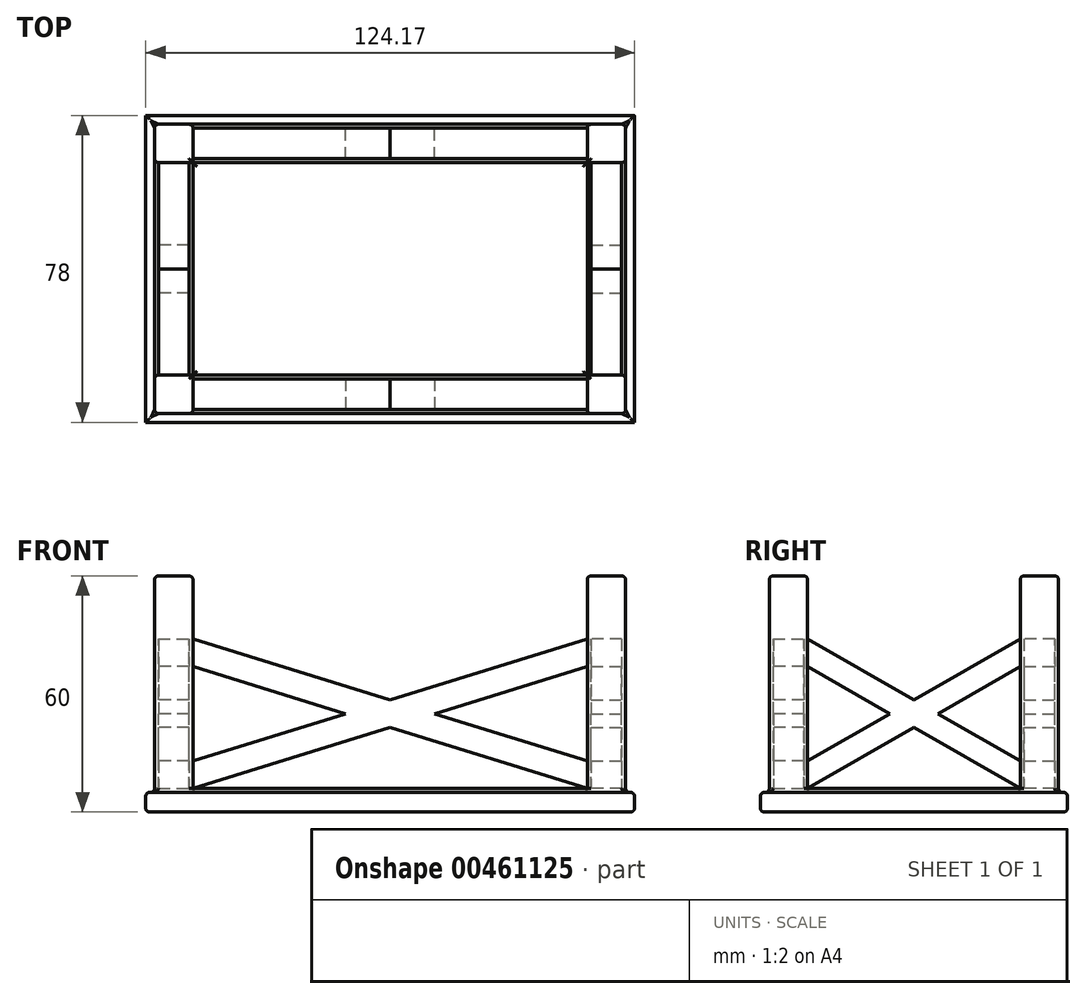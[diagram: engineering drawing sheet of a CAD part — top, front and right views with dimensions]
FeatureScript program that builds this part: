
annotation { "Feature Type Name" : "Feature", "Feature Type Description" : "" }
export const myFeature = defineFeature(function(context is Context, id is Id, definition is map)
    precondition{}
    {
        {
            var Q0;
            Q0=qCreatedBy(makeId("Top.planeOp"),FACE);
            var sketch = newSketch(context, id + "F0", { "sketchPlane" : qUnion([Q0])});
            skLineSegment(sketch, "E0.bottom", {"start": v(-35.73, 48.82) * mm, "end": v(88.44, 48.82) * mm});
            skLineSegment(sketch, "E0.top", {"start": v(-35.73, -29.18) * mm, "end": v(88.44, -29.18) * mm});
            skLineSegment(sketch, "E0.left", {"start": v(-35.73, 48.82) * mm, "end": v(-35.73, -29.18) * mm});
            skLineSegment(sketch, "E0.right", {"start": v(88.44, 48.82) * mm, "end": v(88.44, -29.18) * mm});
            skPoint(sketch, "E1", {"position": v(26.36, -29.18) * mm});
            skSolve(sketch);
        }
        {
            var Q0;
            Q0 = qSketchRegion(id + "F0", true);
            extrude(context, id + "F1", {"entities" : qUnion([Q0]), "depth" : 5 * mm});
        }
        {
            var Q0;
            Q0=makeQuery(id+"F1.opExtrude","CAP_FACE",FACE,{"disambiguationData":[OSD([sQuery(id+"F0.wireOp",EDGE,"E0.bottom"),sQuery(id+"F0.wireOp",EDGE,"E0.top"),sQuery(id+"F0.wireOp",EDGE,"E0.left"),sQuery(id+"F0.wireOp",EDGE,"E0.right")])],"isStart":false});
            var sketch = newSketch(context, id + "F2", { "sketchPlane" : qUnion([Q0])});
            skLineSegment(sketch, "E2.bottom", {"start": v(-35.73, -29.18) * mm, "end": v(-23.73, -29.18) * mm, "construction": true});
            skLineSegment(sketch, "E2.top", {"start": v(-35.73, -17.18) * mm, "end": v(-23.73, -17.18) * mm, "construction": true});
            skLineSegment(sketch, "E2.left", {"start": v(-35.73, -29.18) * mm, "end": v(-35.73, -17.18) * mm, "construction": true});
            skLineSegment(sketch, "E2.right", {"start": v(-23.73, -29.18) * mm, "end": v(-23.73, -17.18) * mm, "construction": true});
            skLineSegment(sketch, "E3.bottom", {"start": v(88.44, 48.82) * mm, "end": v(76.44, 48.82) * mm, "construction": true});
            skLineSegment(sketch, "E3.top", {"start": v(88.44, 36.82) * mm, "end": v(76.44, 36.82) * mm, "construction": true});
            skLineSegment(sketch, "E3.left", {"start": v(88.44, 48.82) * mm, "end": v(88.44, 36.82) * mm, "construction": true});
            skLineSegment(sketch, "E3.right", {"start": v(76.44, 48.82) * mm, "end": v(76.44, 36.82) * mm, "construction": true});
            skLineSegment(sketch, "E4.bottom", {"start": v(88.44, -29.18) * mm, "end": v(76.44, -29.18) * mm, "construction": true});
            skLineSegment(sketch, "E4.top", {"start": v(88.44, -17.18) * mm, "end": v(76.44, -17.18) * mm, "construction": true});
            skLineSegment(sketch, "E4.left", {"start": v(88.44, -29.18) * mm, "end": v(88.44, -17.18) * mm, "construction": true});
            skLineSegment(sketch, "E4.right", {"start": v(76.44, -29.18) * mm, "end": v(76.44, -17.18) * mm, "construction": true});
            skLineSegment(sketch, "E5.bottom", {"start": v(-35.73, 48.82) * mm, "end": v(-23.73, 48.82) * mm, "construction": true});
            skLineSegment(sketch, "E5.top", {"start": v(-35.73, 36.82) * mm, "end": v(-23.73, 36.82) * mm, "construction": true});
            skLineSegment(sketch, "E5.left", {"start": v(-35.73, 48.82) * mm, "end": v(-35.73, 36.82) * mm, "construction": true});
            skLineSegment(sketch, "E5.right", {"start": v(-23.73, 48.82) * mm, "end": v(-23.73, 36.82) * mm, "construction": true});
            skLineSegment(sketch, "E6.bottom", {"start": v(-23.73, 36.82) * mm, "end": v(-33.48, 36.82) * mm});
            skLineSegment(sketch, "E6.top", {"start": v(-23.73, 46.57) * mm, "end": v(-33.48, 46.57) * mm});
            skLineSegment(sketch, "E6.left", {"start": v(-23.73, 36.82) * mm, "end": v(-23.73, 46.57) * mm});
            skLineSegment(sketch, "E6.right", {"start": v(-33.48, 36.82) * mm, "end": v(-33.48, 46.57) * mm});
            skLineSegment(sketch, "E7.bottom", {"start": v(-23.73, -17.18) * mm, "end": v(-33.48, -17.18) * mm});
            skLineSegment(sketch, "E7.top", {"start": v(-23.73, -26.93) * mm, "end": v(-33.48, -26.93) * mm});
            skLineSegment(sketch, "E7.left", {"start": v(-23.73, -17.18) * mm, "end": v(-23.73, -26.93) * mm});
            skLineSegment(sketch, "E7.right", {"start": v(-33.48, -17.18) * mm, "end": v(-33.48, -26.93) * mm});
            skLineSegment(sketch, "E8.bottom", {"start": v(76.44, 36.82) * mm, "end": v(86.2, 36.82) * mm});
            skLineSegment(sketch, "E8.top", {"start": v(76.44, 46.57) * mm, "end": v(86.2, 46.57) * mm});
            skLineSegment(sketch, "E8.left", {"start": v(76.44, 36.82) * mm, "end": v(76.44, 46.57) * mm});
            skLineSegment(sketch, "E8.right", {"start": v(86.2, 36.82) * mm, "end": v(86.2, 46.57) * mm});
            skLineSegment(sketch, "E9.bottom", {"start": v(76.44, -17.18) * mm, "end": v(86.2, -17.18) * mm});
            skLineSegment(sketch, "E9.top", {"start": v(76.44, -26.93) * mm, "end": v(86.2, -26.93) * mm});
            skLineSegment(sketch, "E9.left", {"start": v(76.44, -17.18) * mm, "end": v(76.44, -26.93) * mm});
            skLineSegment(sketch, "E9.right", {"start": v(86.2, -17.18) * mm, "end": v(86.2, -26.93) * mm});
            skSolve(sketch);
        }
        {
            var Q0;
            Q0 = qSketchRegion(id + "F2", true);
            extrude(context, id + "F3", {"entities" : qUnion([Q0]), "operationType" : NewBodyOperationType.ADD, "depth" : 55 * mm});
        }
        {
            var Q0;
            Q0=makeQuery(id+"F3.opExtrude","SWEPT_FACE",FACE,{"disambiguationData":[OSD([sQuery(id+"F2.wireOp",EDGE,"E7.left")])]});
            var sketch = newSketch(context, id + "F4", { "sketchPlane" : qUnion([Q0])});
            skLineSegment(sketch, "E10.bottom", {"start": v(-25.93, 59) * mm, "end": v(-18.18, 59) * mm, "construction": true});
            skLineSegment(sketch, "E10.top", {"start": v(-25.93, 44) * mm, "end": v(-18.18, 44) * mm, "construction": true});
            skLineSegment(sketch, "E10.left", {"start": v(-25.93, 59) * mm, "end": v(-25.93, 44) * mm, "construction": true});
            skLineSegment(sketch, "E10.right", {"start": v(-18.18, 59) * mm, "end": v(-18.18, 44) * mm, "construction": true});
            skLineSegment(sketch, "E11.bottom", {"start": v(-25.93, 44) * mm, "end": v(-18.18, 44) * mm});
            skLineSegment(sketch, "E11.top", {"start": v(-25.93, 6) * mm, "end": v(-18.18, 6) * mm});
            skLineSegment(sketch, "E11.left", {"start": v(-25.93, 44) * mm, "end": v(-25.93, 6) * mm});
            skLineSegment(sketch, "E11.right", {"start": v(-18.18, 44) * mm, "end": v(-18.18, 6) * mm});
            skSolve(sketch);
        }
        {
            var Q0;
            Q0 = qSketchRegion(id + "F4", true);
            extrude(context, id + "F5", {"entities" : qUnion([Q0]), "operationType" : NewBodyOperationType.ADD, "endBound" : BoundingType.UP_TO_NEXT, "depth" : 100.17 * mm});
        }
        {
            var Q0;
            Q0=makeQuery(id+"F5.opExtrude","SWEPT_FACE",FACE,{"disambiguationData":[OSD([sQuery(id+"F4.wireOp",EDGE,"E11.left")])]});
            var sketch = newSketch(context, id + "F6", { "sketchPlane" : qUnion([Q0])});
            skPoint(sketch, "E12", {"position": v(-23.73, 44) * mm});
            skPoint(sketch, "E13", {"position": v(-23.73, 37) * mm});
            skPoint(sketch, "E14", {"position": v(-23.73, 6) * mm});
            skPoint(sketch, "E15", {"position": v(-23.73, 13) * mm});
            skPoint(sketch, "E16", {"position": v(76.44, 44) * mm});
            skPoint(sketch, "E17", {"position": v(76.44, 37) * mm});
            skPoint(sketch, "E18", {"position": v(76.44, 6) * mm});
            skPoint(sketch, "E19", {"position": v(76.44, 13) * mm});
            skPoint(sketch, "E20", {"position": v(26.36, 28.5) * mm});
            skPoint(sketch, "E21", {"position": v(26.36, 21.5) * mm});
            skPoint(sketch, "E22", {"position": v(15.05, 25) * mm});
            skPoint(sketch, "E23", {"position": v(37.67, 25) * mm});
            skLineSegment(sketch, "E24", {"start": v(-23.73, 44) * mm, "end": v(76.44, 44) * mm});
            skLineSegment(sketch, "E25", {"start": v(26.36, 28.5) * mm, "end": v(76.44, 44) * mm});
            skLineSegment(sketch, "E26", {"start": v(-23.73, 44) * mm, "end": v(26.36, 28.5) * mm});
            skLineSegment(sketch, "E27", {"start": v(76.44, 37) * mm, "end": v(76.44, 13) * mm});
            skLineSegment(sketch, "E28", {"start": v(76.44, 13.06) * mm, "end": v(37.67, 25) * mm});
            skLineSegment(sketch, "E29", {"start": v(15.05, 25) * mm, "end": v(-23.73, 37) * mm});
            skLineSegment(sketch, "E30", {"start": v(15.05, 25) * mm, "end": v(-23.73, 13) * mm});
            skLineSegment(sketch, "E31", {"start": v(-23.73, 13) * mm, "end": v(-23.73, 37) * mm});
            skLineSegment(sketch, "E32", {"start": v(-23.73, 6) * mm, "end": v(76.44, 6) * mm});
            skLineSegment(sketch, "E33", {"start": v(26.36, 21.5) * mm, "end": v(76.44, 6) * mm});
            skLineSegment(sketch, "E34", {"start": v(26.36, 21.5) * mm, "end": v(-23.73, 6) * mm});
            skLineSegment(sketch, "E35", {"start": v(37.67, 25) * mm, "end": v(76.44, 37) * mm});
            skLineSegment(sketch, "E36", {"start": v(76.44, 37) * mm, "end": v(76.44, 13.06) * mm});
            skSolve(sketch);
        }
        {
            var Q0;
            Q0 = qSketchRegion(id + "F6", true);
            extrude(context, id + "F7", {"entities" : qUnion([Q0]), "operationType" : NewBodyOperationType.REMOVE, "endBound" : BoundingType.UP_TO_NEXT, "oppositeDirection" : true, "depth" : 25 * mm});
        }
        {
            var Q0;
            Q0=makeQuery(id+"F3.opExtrude","SWEPT_FACE",FACE,{"disambiguationData":[OSD([sQuery(id+"F2.wireOp",EDGE,"E8.left")])]});
            var sketch = newSketch(context, id + "F8", { "sketchPlane" : qUnion([Q0])});
            skLineSegment(sketch, "E37.bottom", {"start": v(-45.57, 59) * mm, "end": v(-37.82, 59) * mm, "construction": true});
            skLineSegment(sketch, "E37.top", {"start": v(-45.57, 44) * mm, "end": v(-37.82, 44) * mm, "construction": true});
            skLineSegment(sketch, "E37.left", {"start": v(-45.57, 59) * mm, "end": v(-45.57, 44) * mm, "construction": true});
            skLineSegment(sketch, "E37.right", {"start": v(-37.82, 59) * mm, "end": v(-37.82, 44) * mm, "construction": true});
            skLineSegment(sketch, "E38.bottom", {"start": v(-45.57, 44) * mm, "end": v(-37.82, 44) * mm});
            skLineSegment(sketch, "E38.top", {"start": v(-45.57, 6) * mm, "end": v(-37.82, 6) * mm});
            skLineSegment(sketch, "E38.left", {"start": v(-45.57, 44) * mm, "end": v(-45.57, 6) * mm});
            skLineSegment(sketch, "E38.right", {"start": v(-37.82, 44) * mm, "end": v(-37.82, 6) * mm});
            skSolve(sketch);
        }
        {
            var Q0;
            Q0 = qSketchRegion(id + "F8", true);
            extrude(context, id + "F9", {"entities" : qUnion([Q0]), "operationType" : NewBodyOperationType.ADD, "endBound" : BoundingType.UP_TO_NEXT, "depth" : 25 * mm});
        }
        {
            var Q0;
            Q0=makeQuery(id+"F9.opExtrude","SWEPT_FACE",FACE,{"disambiguationData":[OSD([sQuery(id+"F8.wireOp",EDGE,"E38.left")])]});
            var sketch = newSketch(context, id + "F10", { "sketchPlane" : qUnion([Q0])});
            skPoint(sketch, "E39", {"position": v(-76.44, 44) * mm});
            skPoint(sketch, "E40", {"position": v(-76.44, 37) * mm});
            skPoint(sketch, "E41", {"position": v(-76.44, 13) * mm});
            skPoint(sketch, "E42", {"position": v(-76.44, 6) * mm});
            skPoint(sketch, "E43", {"position": v(23.73, 44) * mm});
            skPoint(sketch, "E44", {"position": v(23.73, 37) * mm});
            skPoint(sketch, "E45", {"position": v(23.73, 13) * mm});
            skPoint(sketch, "E46", {"position": v(23.73, 6) * mm});
            skLineSegment(sketch, "E47", {"start": v(-76.44, 37) * mm, "end": v(23.73, 6) * mm, "construction": true});
            skLineSegment(sketch, "E48", {"start": v(-76.44, 44) * mm, "end": v(23.73, 13) * mm, "construction": true});
            skLineSegment(sketch, "E49", {"start": v(23.73, 44) * mm, "end": v(-76.44, 13) * mm, "construction": true});
            skLineSegment(sketch, "E50", {"start": v(-76.44, 6) * mm, "end": v(23.73, 37) * mm, "construction": true});
            skLineSegment(sketch, "E51", {"start": v(-76.44, 44) * mm, "end": v(-26.36, 28.5) * mm});
            skLineSegment(sketch, "E52", {"start": v(-26.36, 28.5) * mm, "end": v(23.73, 44) * mm});
            skLineSegment(sketch, "E53", {"start": v(-76.44, 44) * mm, "end": v(23.73, 44) * mm});
            skLineSegment(sketch, "E54", {"start": v(-76.44, 13) * mm, "end": v(-76.44, 37) * mm});
            skLineSegment(sketch, "E55", {"start": v(-76.44, 37) * mm, "end": v(-37.67, 25) * mm});
            skLineSegment(sketch, "E56", {"start": v(-37.67, 25) * mm, "end": v(-76.44, 13) * mm});
            skLineSegment(sketch, "E57", {"start": v(-76.44, 6) * mm, "end": v(23.73, 6) * mm});
            skLineSegment(sketch, "E58", {"start": v(-26.36, 21.5) * mm, "end": v(23.73, 6) * mm});
            skLineSegment(sketch, "E59", {"start": v(-76.44, 6) * mm, "end": v(-26.36, 21.5) * mm});
            skLineSegment(sketch, "E60", {"start": v(23.73, 37) * mm, "end": v(23.73, 13) * mm});
            skLineSegment(sketch, "E61", {"start": v(23.73, 13) * mm, "end": v(-15.05, 25) * mm});
            skLineSegment(sketch, "E62", {"start": v(-15.05, 25) * mm, "end": v(23.73, 37) * mm});
            skSolve(sketch);
        }
        {
            var Q0;
            Q0 = qSketchRegion(id + "F10", true);
            extrude(context, id + "F11", {"entities" : qUnion([Q0]), "operationType" : NewBodyOperationType.REMOVE, "endBound" : BoundingType.UP_TO_NEXT, "oppositeDirection" : true, "depth" : 25 * mm});
        }
        {
            var Q0;
            Q0=makeQuery(id+"F3.opExtrude","SWEPT_FACE",FACE,{"disambiguationData":[OSD([sQuery(id+"F2.wireOp",EDGE,"E6.bottom")])]});
            var sketch = newSketch(context, id + "F12", { "sketchPlane" : qUnion([Q0])});
            skLineSegment(sketch, "E63.bottom", {"start": v(-32.48, 59) * mm, "end": v(-24.73, 59) * mm, "construction": true});
            skLineSegment(sketch, "E63.top", {"start": v(-32.48, 44) * mm, "end": v(-24.73, 44) * mm, "construction": true});
            skLineSegment(sketch, "E63.left", {"start": v(-32.48, 59) * mm, "end": v(-32.48, 44) * mm, "construction": true});
            skLineSegment(sketch, "E63.right", {"start": v(-24.73, 59) * mm, "end": v(-24.73, 44) * mm, "construction": true});
            skLineSegment(sketch, "E64.bottom", {"start": v(-32.48, 44) * mm, "end": v(-24.73, 44) * mm});
            skLineSegment(sketch, "E64.top", {"start": v(-32.48, 6) * mm, "end": v(-24.73, 6) * mm});
            skLineSegment(sketch, "E64.left", {"start": v(-32.48, 44) * mm, "end": v(-32.48, 6) * mm});
            skLineSegment(sketch, "E64.right", {"start": v(-24.73, 44) * mm, "end": v(-24.73, 6) * mm});
            skSolve(sketch);
        }
        {
            var Q0;
            Q0 = qSketchRegion(id + "F12", true);
            extrude(context, id + "F13", {"entities" : qUnion([Q0]), "operationType" : NewBodyOperationType.ADD, "endBound" : BoundingType.UP_TO_NEXT, "depth" : 25 * mm});
        }
        {
            var Q0;
            Q0=makeQuery(id+"F13.opExtrude","SWEPT_FACE",FACE,{"disambiguationData":[OSD([sQuery(id+"F12.wireOp",EDGE,"E64.left")])]});
            var sketch = newSketch(context, id + "F14", { "sketchPlane" : qUnion([Q0])});
            skPoint(sketch, "E65", {"position": v(-36.82, 44) * mm});
            skPoint(sketch, "E66", {"position": v(-36.82, 37) * mm});
            skPoint(sketch, "E67", {"position": v(-36.82, 13) * mm});
            skPoint(sketch, "E68", {"position": v(-36.82, 6) * mm});
            skPoint(sketch, "E69", {"position": v(17.18, 6) * mm});
            skPoint(sketch, "E70", {"position": v(17.18, 13) * mm});
            skPoint(sketch, "E71", {"position": v(17.18, 37) * mm});
            skPoint(sketch, "E72", {"position": v(17.18, 44) * mm});
            skLineSegment(sketch, "E73", {"start": v(-36.82, 37) * mm, "end": v(17.18, 6) * mm, "construction": true});
            skLineSegment(sketch, "E74", {"start": v(17.18, 13) * mm, "end": v(-36.82, 44) * mm, "construction": true});
            skLineSegment(sketch, "E75", {"start": v(-36.82, 13) * mm, "end": v(17.18, 44) * mm, "construction": true});
            skLineSegment(sketch, "E76", {"start": v(17.18, 37) * mm, "end": v(-36.82, 6) * mm, "construction": true});
            skLineSegment(sketch, "E77", {"start": v(-36.82, 44) * mm, "end": v(17.18, 44) * mm});
            skLineSegment(sketch, "E78", {"start": v(-9.82, 28.5) * mm, "end": v(17.18, 44) * mm});
            skLineSegment(sketch, "E79", {"start": v(-9.82, 28.5) * mm, "end": v(-36.82, 44) * mm});
            skLineSegment(sketch, "E80", {"start": v(-36.82, 37) * mm, "end": v(-36.82, 13) * mm});
            skLineSegment(sketch, "E81", {"start": v(-36.82, 13) * mm, "end": v(-15.92, 25) * mm});
            skLineSegment(sketch, "E82", {"start": v(-15.92, 25) * mm, "end": v(-36.82, 37) * mm});
            skLineSegment(sketch, "E83", {"start": v(17.18, 37) * mm, "end": v(17.18, 13) * mm});
            skLineSegment(sketch, "E84", {"start": v(17.18, 13) * mm, "end": v(-3.72, 25) * mm});
            skLineSegment(sketch, "E85", {"start": v(17.18, 37) * mm, "end": v(-3.72, 25) * mm});
            skLineSegment(sketch, "E86", {"start": v(-36.82, 6) * mm, "end": v(17.18, 6) * mm});
            skLineSegment(sketch, "E87", {"start": v(17.18, 6) * mm, "end": v(-9.82, 21.5) * mm});
            skLineSegment(sketch, "E88", {"start": v(-36.82, 6) * mm, "end": v(-9.82, 21.5) * mm});
            skSolve(sketch);
        }
        {
            var Q0;
            Q0 = qSketchRegion(id + "F14", true);
            extrude(context, id + "F15", {"entities" : qUnion([Q0]), "operationType" : NewBodyOperationType.REMOVE, "endBound" : BoundingType.UP_TO_NEXT, "oppositeDirection" : true, "depth" : 25 * mm});
        }
        {
            var Q0;
            Q0=makeQuery(id+"F3.opExtrude","SWEPT_FACE",FACE,{"disambiguationData":[OSD([sQuery(id+"F2.wireOp",EDGE,"E9.bottom")])]});
            var sketch = newSketch(context, id + "F16", { "sketchPlane" : qUnion([Q0])});
            skLineSegment(sketch, "E89.bottom", {"start": v(-85.2, 59) * mm, "end": v(-77.44, 59) * mm, "construction": true});
            skLineSegment(sketch, "E89.top", {"start": v(-85.2, 44) * mm, "end": v(-77.44, 44) * mm, "construction": true});
            skLineSegment(sketch, "E89.left", {"start": v(-85.2, 59) * mm, "end": v(-85.2, 44) * mm, "construction": true});
            skLineSegment(sketch, "E89.right", {"start": v(-77.44, 59) * mm, "end": v(-77.44, 44) * mm, "construction": true});
            skLineSegment(sketch, "E90.bottom", {"start": v(-85.2, 44) * mm, "end": v(-77.44, 44) * mm});
            skLineSegment(sketch, "E90.top", {"start": v(-85.2, 6) * mm, "end": v(-77.44, 6) * mm});
            skLineSegment(sketch, "E90.left", {"start": v(-85.2, 44) * mm, "end": v(-85.2, 6) * mm});
            skLineSegment(sketch, "E90.right", {"start": v(-77.44, 44) * mm, "end": v(-77.44, 6) * mm});
            skSolve(sketch);
        }
        {
            var Q0;
            Q0 = qSketchRegion(id + "F16", true);
            extrude(context, id + "F17", {"entities" : qUnion([Q0]), "operationType" : NewBodyOperationType.ADD, "endBound" : BoundingType.UP_TO_NEXT, "depth" : 25 * mm});
        }
        {
            var Q0;
            Q0=makeQuery(id+"F17.opExtrude","SWEPT_FACE",FACE,{"disambiguationData":[OSD([sQuery(id+"F16.wireOp",EDGE,"E90.left")])]});
            var sketch = newSketch(context, id + "F18", { "sketchPlane" : qUnion([Q0])});
            skPoint(sketch, "E91", {"position": v(-17.18, 44) * mm});
            skPoint(sketch, "E92", {"position": v(-17.18, 37) * mm});
            skPoint(sketch, "E93", {"position": v(-17.18, 13) * mm});
            skPoint(sketch, "E94", {"position": v(-17.18, 6) * mm});
            skPoint(sketch, "E95", {"position": v(36.82, 44) * mm});
            skPoint(sketch, "E96", {"position": v(36.82, 37) * mm});
            skPoint(sketch, "E97", {"position": v(36.82, 13) * mm});
            skPoint(sketch, "E98", {"position": v(36.82, 6) * mm});
            skLineSegment(sketch, "E99", {"start": v(-17.18, 44) * mm, "end": v(36.82, 13) * mm, "construction": true});
            skLineSegment(sketch, "E100", {"start": v(36.82, 6) * mm, "end": v(-17.18, 37) * mm, "construction": true});
            skLineSegment(sketch, "E101", {"start": v(36.82, 44) * mm, "end": v(-17.18, 13) * mm, "construction": true});
            skLineSegment(sketch, "E102", {"start": v(-17.18, 6) * mm, "end": v(36.82, 37) * mm, "construction": true});
            skLineSegment(sketch, "E103", {"start": v(-17.18, 44) * mm, "end": v(36.82, 44) * mm});
            skLineSegment(sketch, "E104", {"start": v(36.82, 44) * mm, "end": v(9.82, 28.5) * mm});
            skLineSegment(sketch, "E105", {"start": v(9.82, 28.5) * mm, "end": v(-17.18, 44) * mm});
            skLineSegment(sketch, "E106", {"start": v(-17.18, 37) * mm, "end": v(-17.18, 13) * mm});
            skLineSegment(sketch, "E107", {"start": v(-17.18, 13) * mm, "end": v(3.72, 25) * mm});
            skLineSegment(sketch, "E108", {"start": v(-17.18, 37) * mm, "end": v(3.72, 25) * mm});
            skLineSegment(sketch, "E109", {"start": v(36.82, 37) * mm, "end": v(36.82, 13) * mm});
            skLineSegment(sketch, "E110", {"start": v(36.82, 13) * mm, "end": v(15.92, 25) * mm});
            skLineSegment(sketch, "E111", {"start": v(15.92, 25) * mm, "end": v(36.82, 37) * mm});
            skLineSegment(sketch, "E112", {"start": v(-17.18, 6) * mm, "end": v(36.82, 6) * mm});
            skLineSegment(sketch, "E113", {"start": v(36.82, 6) * mm, "end": v(9.82, 21.5) * mm});
            skLineSegment(sketch, "E114", {"start": v(9.82, 21.5) * mm, "end": v(-17.18, 6) * mm});
            skSolve(sketch);
        }
        {
            var Q0;
            Q0 = qSketchRegion(id + "F18", true);
            extrude(context, id + "F19", {"entities" : qUnion([Q0]), "operationType" : NewBodyOperationType.REMOVE, "endBound" : BoundingType.UP_TO_NEXT, "oppositeDirection" : true, "depth" : 25 * mm});
        }
        {
            var Q0;
            Q0=makeQuery(id+"F15.boolean.opBoolean","MERGE",FACE,{"derivedFrom":[makeQuery(id+"F3.opExtrude","SWEPT_FACE",FACE,{"disambiguationData":[OSD([sQuery(id+"F2.wireOp",EDGE,"E7.bottom")])]}),makeQuery(id+"F15.opExtrude","SWEPT_FACE",FACE,{"disambiguationData":[OSD([sQuery(id+"F14.wireOp",EDGE,"E83")])]})]});
            var sketch = newSketch(context, id + "F20", { "sketchPlane" : qUnion([Q0])});
            skLineSegment(sketch, "E115.bottom", {"start": v(33.48, 5) * mm, "end": v(23.73, 5) * mm});
            skLineSegment(sketch, "E115.top", {"start": v(33.48, 6) * mm, "end": v(23.73, 6) * mm});
            skLineSegment(sketch, "E115.left", {"start": v(33.48, 5) * mm, "end": v(33.48, 6) * mm});
            skLineSegment(sketch, "E115.right", {"start": v(23.73, 5) * mm, "end": v(23.73, 6) * mm});
            skSolve(sketch);
        }
        {
            var Q0;
            Q0 = qSketchRegion(id + "F20", true);
            extrude(context, id + "F21", {"entities" : qUnion([Q0]), "operationType" : NewBodyOperationType.ADD, "endBound" : BoundingType.UP_TO_NEXT, "depth" : 25 * mm});
        }
        {
            var Q0;
            Q0=makeQuery(id+"F21.boolean.opBoolean","MERGE",FACE,{"derivedFrom":[makeQuery(id+"F7.boolean.opBoolean","MERGE",FACE,{"derivedFrom":[makeQuery(id+"F3.opExtrude","SWEPT_FACE",FACE,{"disambiguationData":[OSD([sQuery(id+"F2.wireOp",EDGE,"E7.left")])]}),makeQuery(id+"F7.opExtrude","SWEPT_FACE",FACE,{"disambiguationData":[OSD([sQuery(id+"F6.wireOp",EDGE,"E31")])]})]}),makeQuery(id+"F11.boolean.opBoolean","MERGE",FACE,{"derivedFrom":[makeQuery(id+"F3.opExtrude","SWEPT_FACE",FACE,{"disambiguationData":[OSD([sQuery(id+"F2.wireOp",EDGE,"E6.left")])]}),makeQuery(id+"F11.opExtrude","SWEPT_FACE",FACE,{"disambiguationData":[OSD([sQuery(id+"F10.wireOp",EDGE,"E60")])]})]}),makeQuery(id+"F21.opExtrude","SWEPT_FACE",FACE,{"disambiguationData":[OSD([sQuery(id+"F20.wireOp",EDGE,"E115.right")])]})]});
            var sketch = newSketch(context, id + "F22", { "sketchPlane" : qUnion([Q0])});
            skLineSegment(sketch, "E116.bottom", {"start": v(46.57, 5) * mm, "end": v(36.82, 5) * mm});
            skLineSegment(sketch, "E116.top", {"start": v(46.57, 6) * mm, "end": v(36.82, 6) * mm});
            skLineSegment(sketch, "E116.left", {"start": v(46.57, 5) * mm, "end": v(46.57, 6) * mm});
            skLineSegment(sketch, "E116.right", {"start": v(36.82, 5) * mm, "end": v(36.82, 6) * mm});
            skSolve(sketch);
        }
        {
            var Q0;
            Q0 = qSketchRegion(id + "F22", true);
            extrude(context, id + "F23", {"entities" : qUnion([Q0]), "operationType" : NewBodyOperationType.ADD, "endBound" : BoundingType.UP_TO_NEXT, "depth" : 25 * mm});
        }
        {
            var Q0;
            Q0=makeQuery(id+"F23.boolean.opBoolean","MERGE",FACE,{"derivedFrom":[makeQuery(id+"F19.boolean.opBoolean","MERGE",FACE,{"derivedFrom":[makeQuery(id+"F3.opExtrude","SWEPT_FACE",FACE,{"disambiguationData":[OSD([sQuery(id+"F2.wireOp",EDGE,"E8.bottom")])]}),makeQuery(id+"F19.opExtrude","SWEPT_FACE",FACE,{"disambiguationData":[OSD([sQuery(id+"F18.wireOp",EDGE,"E109")])]})]}),makeQuery(id+"F23.opExtrude","SWEPT_FACE",FACE,{"disambiguationData":[OSD([sQuery(id+"F22.wireOp",EDGE,"E116.right")])]})]});
            var sketch = newSketch(context, id + "F24", { "sketchPlane" : qUnion([Q0])});
            skLineSegment(sketch, "E117.bottom", {"start": v(86.2, 5) * mm, "end": v(76.44, 5) * mm});
            skLineSegment(sketch, "E117.top", {"start": v(86.2, 6) * mm, "end": v(76.44, 6) * mm});
            skLineSegment(sketch, "E117.left", {"start": v(86.2, 5) * mm, "end": v(86.2, 6) * mm});
            skLineSegment(sketch, "E117.right", {"start": v(76.44, 5) * mm, "end": v(76.44, 6) * mm});
            skSolve(sketch);
        }
        {
            var Q0;
            Q0 = qSketchRegion(id + "F24", true);
            extrude(context, id + "F25", {"entities" : qUnion([Q0]), "operationType" : NewBodyOperationType.ADD, "endBound" : BoundingType.UP_TO_NEXT, "depth" : 25 * mm});
        }
        {
            var Q0;
            Q0=makeQuery(id+"F25.boolean.opBoolean","MERGE",FACE,{"derivedFrom":[makeQuery(id+"F3.opExtrude","SWEPT_FACE",FACE,{"disambiguationData":[OSD([sQuery(id+"F2.wireOp",EDGE,"E9.left")])]}),makeQuery(id+"F25.opExtrude","SWEPT_FACE",FACE,{"disambiguationData":[OSD([sQuery(id+"F24.wireOp",EDGE,"E117.right")])]})]});
            var sketch = newSketch(context, id + "F26", { "sketchPlane" : qUnion([Q0])});
            skLineSegment(sketch, "E118.bottom", {"start": v(26.93, 5) * mm, "end": v(17.18, 5) * mm});
            skLineSegment(sketch, "E118.top", {"start": v(26.93, 6) * mm, "end": v(17.18, 6) * mm});
            skLineSegment(sketch, "E118.left", {"start": v(26.93, 5) * mm, "end": v(26.93, 6) * mm});
            skLineSegment(sketch, "E118.right", {"start": v(17.18, 5) * mm, "end": v(17.18, 6) * mm});
            skSolve(sketch);
        }
        {
            var Q0;
            Q0 = qSketchRegion(id + "F26", true);
            extrude(context, id + "F27", {"entities" : qUnion([Q0]), "operationType" : NewBodyOperationType.ADD, "endBound" : BoundingType.UP_TO_NEXT, "depth" : 25 * mm});
        }
        {
            var Q0;
            Q0=makeQuery(id+"F1.opExtrude","CAP_FACE",FACE,{"disambiguationData":[OSD([sQuery(id+"F0.wireOp",EDGE,"E0.bottom"),sQuery(id+"F0.wireOp",EDGE,"E0.top"),sQuery(id+"F0.wireOp",EDGE,"E0.left"),sQuery(id+"F0.wireOp",EDGE,"E0.right")])],"isStart":true});
            var Q1;
            Q1=makeQuery(id+"F27.boolean.opBoolean","SPLIT",FACE,{"disambiguationData":[TD([makeQuery(id+"F3.opExtrude","SWEPT_FACE",FACE,{"disambiguationData":[OSD([sQuery(id+"F2.wireOp",EDGE,"E6.left")])]})])],"derivedFrom":makeQuery(id+"F1.opExtrude","CAP_FACE",FACE,{"disambiguationData":[OSD([sQuery(id+"F0.wireOp",EDGE,"E0.bottom"),sQuery(id+"F0.wireOp",EDGE,"E0.top"),sQuery(id+"F0.wireOp",EDGE,"E0.left"),sQuery(id+"F0.wireOp",EDGE,"E0.right")])],"isStart":false})});
            var Q2;
            {var subQ0=sQuery(id+"F0.wireOp",EDGE,"E0.bottom");var subQ1=sQuery(id+"F0.wireOp",EDGE,"E0.right");var subQ2=sQuery(id+"F0.wireOp",EDGE,"E0.top");var subQ3=sQuery(id+"F0.wireOp",EDGE,"E0.left");Q2=makeQuery(id+"F27.boolean.opBoolean","SPLIT",FACE,{"disambiguationData":[TD([makeQuery(id+"F1.opExtrude","SWEPT_FACE",FACE,{"disambiguationData":[OSD([subQ0])]})])],"derivedFrom":makeQuery(id+"F1.opExtrude","CAP_FACE",FACE,{"disambiguationData":[OSD([subQ0,subQ2,subQ3,subQ1])],"isStart":false})});}
            var Q3;
            Q3=makeQuery(id+"F3.opExtrude","CAP_FACE",FACE,{"disambiguationData":[OSD([sQuery(id+"F2.wireOp",EDGE,"E8.bottom"),sQuery(id+"F2.wireOp",EDGE,"E8.top"),sQuery(id+"F2.wireOp",EDGE,"E8.left"),sQuery(id+"F2.wireOp",EDGE,"E8.right")])],"isStart":false});
            var Q4;
            Q4=makeQuery(id+"F3.opExtrude","CAP_FACE",FACE,{"disambiguationData":[OSD([sQuery(id+"F2.wireOp",EDGE,"E7.bottom"),sQuery(id+"F2.wireOp",EDGE,"E7.top"),sQuery(id+"F2.wireOp",EDGE,"E7.left"),sQuery(id+"F2.wireOp",EDGE,"E7.right")])],"isStart":false});
            var Q5;
            Q5=makeQuery(id+"F3.opExtrude","CAP_FACE",FACE,{"disambiguationData":[OSD([sQuery(id+"F2.wireOp",EDGE,"E6.bottom"),sQuery(id+"F2.wireOp",EDGE,"E6.top"),sQuery(id+"F2.wireOp",EDGE,"E6.left"),sQuery(id+"F2.wireOp",EDGE,"E6.right")])],"isStart":false});
            var Q6;
            Q6=makeQuery(id+"F3.opExtrude","CAP_FACE",FACE,{"disambiguationData":[OSD([sQuery(id+"F2.wireOp",EDGE,"E9.bottom"),sQuery(id+"F2.wireOp",EDGE,"E9.top"),sQuery(id+"F2.wireOp",EDGE,"E9.left"),sQuery(id+"F2.wireOp",EDGE,"E9.right")])],"isStart":false});
            fillet(context, id + "F28", {"entities" : qUnion([Q0, Q1, Q2, Q3, Q4, Q5, Q6]), "radius" : 1 * mm, "tangentPropagation" : true, "allowEdgeOverflow" : false});
        }
        {
            var Q0;
            Q0=makeQuery(id+"F28.opFillet","SPLIT",FACE,{"disambiguationData":[OD(1.0)],"derivedFrom":makeQuery(id+"F25.boolean.opBoolean","MERGE",FACE,{"derivedFrom":[makeQuery(id+"F3.opExtrude","SWEPT_FACE",FACE,{"disambiguationData":[OSD([sQuery(id+"F2.wireOp",EDGE,"E8.right")])]}),makeQuery(id+"F3.opExtrude","SWEPT_FACE",FACE,{"disambiguationData":[OSD([sQuery(id+"F2.wireOp",EDGE,"E9.right")])]}),makeQuery(id+"F25.opExtrude","SWEPT_FACE",FACE,{"disambiguationData":[OSD([sQuery(id+"F24.wireOp",EDGE,"E117.left")])]})]})});
            var Q1;
            Q1=makeQuery(id+"F28.opFillet","SPLIT",FACE,{"disambiguationData":[OD(1.0)],"derivedFrom":makeQuery(id+"F27.boolean.opBoolean","MERGE",FACE,{"derivedFrom":[makeQuery(id+"F3.opExtrude","SWEPT_FACE",FACE,{"disambiguationData":[OSD([sQuery(id+"F2.wireOp",EDGE,"E7.top")])]}),makeQuery(id+"F3.opExtrude","SWEPT_FACE",FACE,{"disambiguationData":[OSD([sQuery(id+"F2.wireOp",EDGE,"E9.top")])]}),makeQuery(id+"F27.opExtrude","SWEPT_FACE",FACE,{"disambiguationData":[OSD([sQuery(id+"F26.wireOp",EDGE,"E118.left")])]})]})});
            var Q2;
            Q2=makeQuery(id+"F28.opFillet","SPLIT",FACE,{"disambiguationData":[OD(0.0)],"derivedFrom":makeQuery(id+"F27.boolean.opBoolean","MERGE",FACE,{"derivedFrom":[makeQuery(id+"F3.opExtrude","SWEPT_FACE",FACE,{"disambiguationData":[OSD([sQuery(id+"F2.wireOp",EDGE,"E7.top")])]}),makeQuery(id+"F3.opExtrude","SWEPT_FACE",FACE,{"disambiguationData":[OSD([sQuery(id+"F2.wireOp",EDGE,"E9.top")])]}),makeQuery(id+"F27.opExtrude","SWEPT_FACE",FACE,{"disambiguationData":[OSD([sQuery(id+"F26.wireOp",EDGE,"E118.left")])]})]})});
            var Q3;
            Q3=makeQuery(id+"F28.opFillet","SPLIT",FACE,{"disambiguationData":[OD(1.0)],"derivedFrom":makeQuery(id+"F21.boolean.opBoolean","MERGE",FACE,{"derivedFrom":[makeQuery(id+"F3.opExtrude","SWEPT_FACE",FACE,{"disambiguationData":[OSD([sQuery(id+"F2.wireOp",EDGE,"E6.right")])]}),makeQuery(id+"F3.opExtrude","SWEPT_FACE",FACE,{"disambiguationData":[OSD([sQuery(id+"F2.wireOp",EDGE,"E7.right")])]}),makeQuery(id+"F21.opExtrude","SWEPT_FACE",FACE,{"disambiguationData":[OSD([sQuery(id+"F20.wireOp",EDGE,"E115.left")])]})]})});
            var Q4;
            Q4=makeQuery(id+"F28.opFillet","SPLIT",FACE,{"disambiguationData":[OD(0.0)],"derivedFrom":makeQuery(id+"F21.boolean.opBoolean","MERGE",FACE,{"derivedFrom":[makeQuery(id+"F3.opExtrude","SWEPT_FACE",FACE,{"disambiguationData":[OSD([sQuery(id+"F2.wireOp",EDGE,"E6.right")])]}),makeQuery(id+"F3.opExtrude","SWEPT_FACE",FACE,{"disambiguationData":[OSD([sQuery(id+"F2.wireOp",EDGE,"E7.right")])]}),makeQuery(id+"F21.opExtrude","SWEPT_FACE",FACE,{"disambiguationData":[OSD([sQuery(id+"F20.wireOp",EDGE,"E115.left")])]})]})});
            var Q5;
            Q5=makeQuery(id+"F28.opFillet","SPLIT",FACE,{"disambiguationData":[OD(0.0)],"derivedFrom":makeQuery(id+"F23.boolean.opBoolean","MERGE",FACE,{"derivedFrom":[makeQuery(id+"F3.opExtrude","SWEPT_FACE",FACE,{"disambiguationData":[OSD([sQuery(id+"F2.wireOp",EDGE,"E6.top")])]}),makeQuery(id+"F3.opExtrude","SWEPT_FACE",FACE,{"disambiguationData":[OSD([sQuery(id+"F2.wireOp",EDGE,"E8.top")])]}),makeQuery(id+"F23.opExtrude","SWEPT_FACE",FACE,{"disambiguationData":[OSD([sQuery(id+"F22.wireOp",EDGE,"E116.left")])]})]})});
            var Q6;
            Q6=makeQuery(id+"F28.opFillet","SPLIT",FACE,{"disambiguationData":[OD(1.0)],"derivedFrom":makeQuery(id+"F23.boolean.opBoolean","MERGE",FACE,{"derivedFrom":[makeQuery(id+"F3.opExtrude","SWEPT_FACE",FACE,{"disambiguationData":[OSD([sQuery(id+"F2.wireOp",EDGE,"E6.top")])]}),makeQuery(id+"F3.opExtrude","SWEPT_FACE",FACE,{"disambiguationData":[OSD([sQuery(id+"F2.wireOp",EDGE,"E8.top")])]}),makeQuery(id+"F23.opExtrude","SWEPT_FACE",FACE,{"disambiguationData":[OSD([sQuery(id+"F22.wireOp",EDGE,"E116.left")])]})]})});
            var Q7;
            Q7=makeQuery(id+"F28.opFillet","SPLIT",FACE,{"disambiguationData":[OD(0.0)],"derivedFrom":makeQuery(id+"F25.boolean.opBoolean","MERGE",FACE,{"derivedFrom":[makeQuery(id+"F3.opExtrude","SWEPT_FACE",FACE,{"disambiguationData":[OSD([sQuery(id+"F2.wireOp",EDGE,"E8.right")])]}),makeQuery(id+"F3.opExtrude","SWEPT_FACE",FACE,{"disambiguationData":[OSD([sQuery(id+"F2.wireOp",EDGE,"E9.right")])]}),makeQuery(id+"F25.opExtrude","SWEPT_FACE",FACE,{"disambiguationData":[OSD([sQuery(id+"F24.wireOp",EDGE,"E117.left")])]})]})});
            fillet(context, id + "F29", {"entities" : qUnion([Q0, Q1, Q2, Q3, Q4, Q5, Q6, Q7]), "radius" : 1 * mm, "tangentPropagation" : true, "allowEdgeOverflow" : false});
        }
    });
